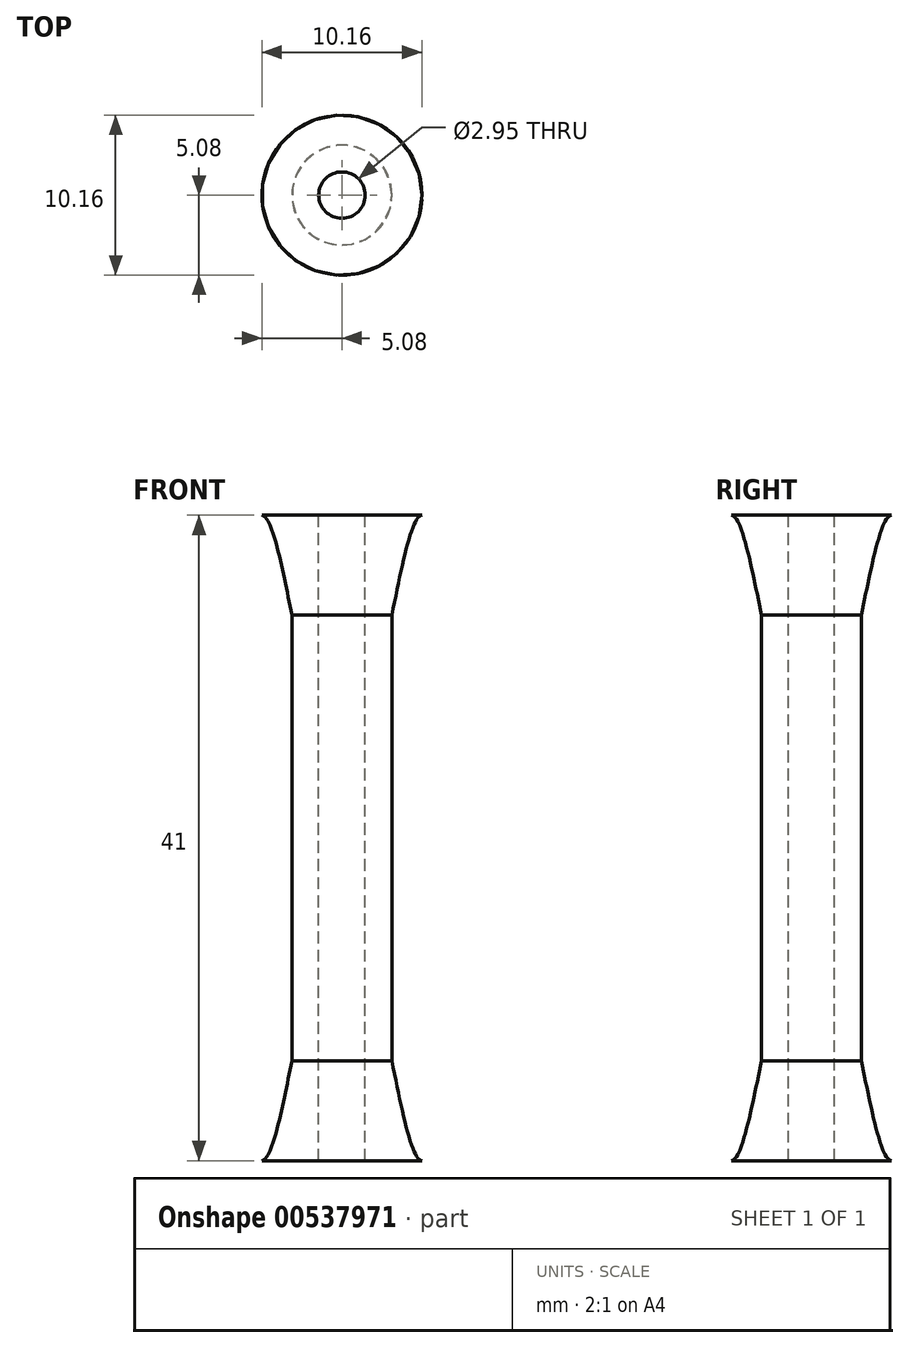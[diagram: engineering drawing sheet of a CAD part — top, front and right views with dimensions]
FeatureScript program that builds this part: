
annotation { "Feature Type Name" : "Feature", "Feature Type Description" : "" }
export const myFeature = defineFeature(function(context is Context, id is Id, definition is map)
    precondition{}
    {
        {
            var Q0;
            Q0=qCreatedBy(makeId("Top.planeOp"),FACE);
            var sketch = newSketch(context, id + "F0", { "sketchPlane" : qUnion([Q0])});
            skCircle(sketch, "E0", {"center": v(0, 0) * mm, "radius": 1.45 * mm});
            skCircle(sketch, "E1", {"center": v(0, 0) * mm, "radius": 3.17 * mm});
            skSolve(sketch);
        }
        {
            var Q0;
            Q0=qCreatedBy(makeId("Top.planeOp"),FACE);
            cPlane(context, id + "F1", {"entities" : qUnion([Q0]), "cplaneType" : CPlaneType.OFFSET, "offset" : 6.35 * mm, "oppositeDirection" : true, "width" : 152.4 * mm, "height" : 152.4 * mm});
        }
        {
            var Q0;
            Q0=qCreatedBy(makeId("Top.planeOp"),FACE);
            cPlane(context, id + "F2", {"entities" : qUnion([Q0]), "cplaneType" : CPlaneType.OFFSET, "offset" : 14.15 * mm, "width" : 152.4 * mm, "height" : 152.4 * mm});
        }
        {
            var Q0;
            Q0=qCreatedBy(id+"F1.planeOp",FACE);
            var sketch = newSketch(context, id + "F3", { "sketchPlane" : qUnion([Q0])});
            skCircle(sketch, "E2", {"center": v(0, 0) * mm, "radius": 5.08 * mm});
            skSolve(sketch);
        }
        {
            var Q0;
            Q0=makeQuery(id+"F0.imprint","IMPRINT",FACE,{"disambiguationData":[TD([[makeQuery(id+"F0.imprint","IMPRINT",EDGE,{"derivedFrom":sQuery(id+"F0.wireOp",EDGE,"E0")}),-1.0]])]});
            var Q1;
            Q1=makeQuery(id+"F0.imprint","IMPRINT",FACE,{"disambiguationData":[TD([[makeQuery(id+"F0.imprint","IMPRINT",EDGE,{"derivedFrom":sQuery(id+"F0.wireOp",EDGE,"E0")}),1.0]])]});
            var Q2;
            Q2=qCreatedBy(id+"F2.planeOp",FACE);
            extrude(context, id + "F4", {"entities" : qUnion([Q0, Q1]), "endBound" : BoundingType.UP_TO_SURFACE, "depth" : 25.4 * mm, "endBoundEntityFace" : qUnion([Q2]), "offsetDistance" : 25.4 * mm});
        }
        {
            var Q1;
            Q1=makeQuery(id+"F4.opExtrude","CAP_FACE",FACE,{"disambiguationData":[OSD([sQuery(id+"F0.wireOp",EDGE,"E1")])],"isStart":true});
            var Q2;
            Q2=makeQuery(id+"F3.imprint","IMPRINT",FACE,{"disambiguationData":[TD([[makeQuery(id+"F3.imprint","IMPRINT",EDGE,{"derivedFrom":sQuery(id+"F3.wireOp",EDGE,"E2")}),1.0]])]});
            loft(context, id + "F5", {"operationType" : NewBodyOperationType.ADD, "endCondition" : LoftEndDerivativeType.TANGENT_TO_PROFILE, "endMagnitude" : 1, "sheetProfilesArray" : [{ "sheetProfileEntities" : qUnion([Q1]) }, { "sheetProfileEntities" : qUnion([Q2]) }]});
        }
        {
            var Q0;
            Q0=makeQuery(id+"F4.opExtrude","SWEPT_BODY",BODY,{"disambiguationData":[OSD([sQuery(id+"F0.wireOp",EDGE,"E1")])]});
            var Q1;
            Q1=qCreatedBy(id+"F2.planeOp",FACE);
            mirror(context, id + "F6", {"operationType" : NewBodyOperationType.ADD, "entities" : qUnion([Q0]), "mirrorPlane" : qUnion([Q1])});
        }
        {
            var Q0;
            Q0=makeQuery(id+"F6.opPattern","COPY",FACE,{"derivedFrom":makeQuery(id+"F5.opLoft","CAP_FACE",FACE,{"disambiguationData":[OSD([makeQuery(id+"F3.imprint","IMPRINT",FACE,{"disambiguationData":[TD([[makeQuery(id+"F3.imprint","IMPRINT",EDGE,{"derivedFrom":sQuery(id+"F3.wireOp",EDGE,"E2")}),1.0]])]})])],"isStart":true}),"instanceName":"1"});
            var sketch = newSketch(context, id + "F7", { "sketchPlane" : qUnion([Q0])});
            skCircle(sketch, "E3", {"center": v(0, 0) * mm, "radius": 2.37 * mm});
            skSolve(sketch);
        }
        {
            var Q0;
            Q0=sQuery(id+"F7.wireOp",VERTEX,"E3.center");
            var Q1;
            Q1=makeQuery(id+"F4.opExtrude","SWEPT_BODY",BODY,{"disambiguationData":[OSD([sQuery(id+"F0.wireOp",EDGE,"E1")])]});
            hole(context, id + "F8", {"style" : HoleStyle.SIMPLE, "endStyle" : HoleEndStyle.THROUGH, "standardTappedOrClearance" : lookupTablePath({ "standard" : "ANSI", "fit" : "Close", "size" : "#4", "type" : "Clearance" }), "standardBlindInLast" : lookupTablePath({ "fit" : "Close", "standard" : "ANSI", "size" : "#4", "type" : "Clearance" }), "holeDiameter" : 2.95 * mm, "majorDiameter" : 6.35 * mm, "isTappedThrough" : true, "tappedDepth" : 12.7 * mm, "tapClearance" : 3, "locations" : qUnion([Q0]), "scope" : qUnion([Q1])});
        }
    });
